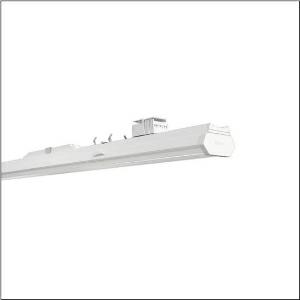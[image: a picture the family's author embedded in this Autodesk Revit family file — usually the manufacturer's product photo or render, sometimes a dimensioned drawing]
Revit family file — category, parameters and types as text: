
# Revit family: licross_r__21_protected_mo_52td12dn4a5gd_b3fc
name_source: partatom
category: Lighting Fixtures
units: mm (PartAtom-declared; Revit-internal decimal feet)

## family parameters
Cut with Voids When Loaded = No
Host = Face
Light Source = No
Part Type = Normal
Room Calculation Point = No
Round Connector Dimension = Use Diameter
Shared = No

## types (1)
- --- (1 x LED, 1610 lm, 10.2 W, 4000K)
    Apparent Load = 10 VA
    CIE Flux Codes = 73 92 98 99 100
    Color Rendering = 80
    Color Temperature = 4000K
    Default Elevation = 1800 mm
    Description = Licross® 21 Protected MO, luminaire insert, of sheet steel, galvanised, coil coated, white, length: 1.500mm, width: 90mm, height: 103mm, LED rated luminous flux: 10.700lm, light colour: 840, control gear: DALI 2 (for two DALI lines), with plug, 6-pole, with phase selection, mains connection: 220..240V, AC/DC, 0/50..60Hz, rated input power: 62W, without changeover relay, for emergency light function, for central battery installations according to DIN EN 60598-2-22, internal wiring halogen-free, primary light control with lens, of plastic, primary optical cover: cover, of PMMA, light emission: direct distribution, primary light characteristic: symmetric, protection rating (complete): IP54, insulation class (complete): insulation class I (protective earthing), certification: CE, ENEC, VDE, UKCA, protection symbol: D if used in an environment with non-conductive dust loads with corresponding accessories, impact resistance: IK06, permissible ambient temperature for indoor applications: -25..+35°C, standard: EN 60598-2-22, corresponds to IFS (International Featured Standards) requirements for safety and quality in the food industry, reducing of maximum allowable ambient temperature of 5°C with ceiling mounting, LABS conformity tested according to VDMA 24364:2018-05, packaging unit: 1 piece
    Height = 92 mm
    Lamp = 1 x LED
    Lamp Light Flux = 1610 lm
    Lamp Power = 10.2 W
    Lamp count = 1
    Length = 1500 mm
    Luminous efficacy = 158 lm/W
    Manufacturer = Siteco
    ModVariant = No
    Model = 52TD12DN4A5GD
    Mounting Place = Ceiling
    Mounting Type = Pendant
    Number of Poles = 1
    OnlyDefault = Yes
    Power Factor = 1
    Product Name = Licross® 21 Protected MO
    Product group = luminaire insert | ceiling pendant
    ProductGroupID = 902
    Protection Class = Protection class I
    Protection Degree = IP 54
    RLX_Detail_Level = 1
    RLX_Emergency_Light_Flux = 0 lm
    RLX_Emergency_Type = 0
    RLX_Emergency_Type_DB = No
    RlxData = <blob elided: 24925 chars, md5=a42a5a11>
    Socket = socket
    Standby Power = 0 W
    System Light Flux = 1610 lm
    System Power = 10 W
    Type Comments = : DC mode (central or group accumulator) initial emergency light level
    Type Image = l_1256148.jpg
    URL = http://relux.com
    VarID = @adj_137781
    Voltage = 0 V
    Weight = 0.00 kg
    Width = 88 mm

## geometry (parser evidence)
native form markers: Blend x4, Sweep x11
no freeform markers — native parametric forms only
